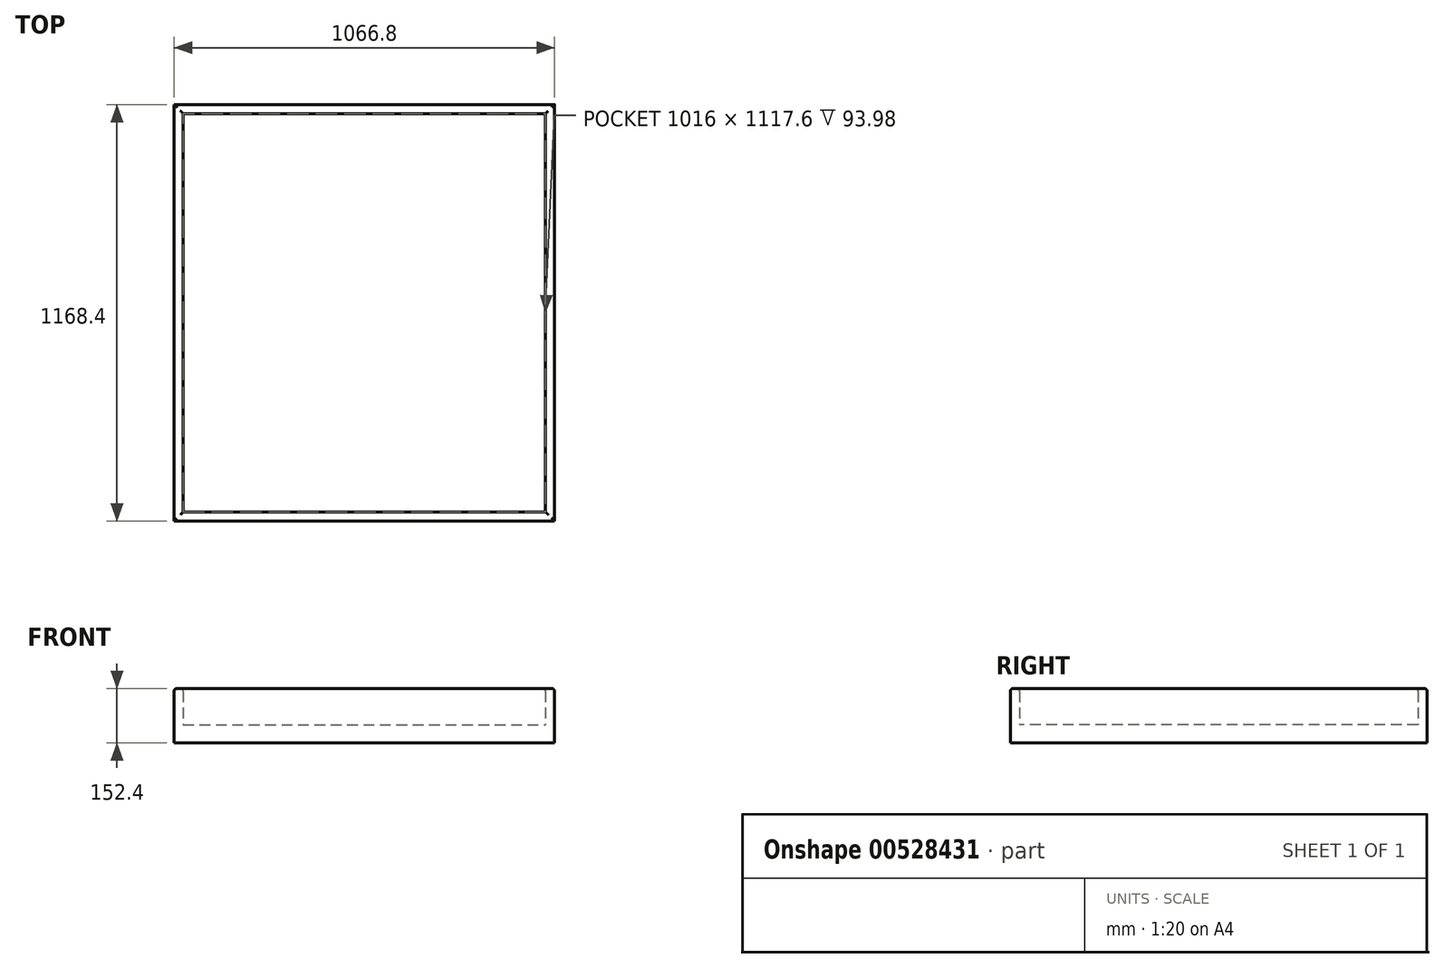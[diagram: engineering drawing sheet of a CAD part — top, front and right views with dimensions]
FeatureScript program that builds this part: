
annotation { "Feature Type Name" : "Feature", "Feature Type Description" : "" }
export const myFeature = defineFeature(function(context is Context, id is Id, definition is map)
    precondition{}
    {
        {
            var Q0;
            Q0=qCreatedBy(makeId("Top.planeOp"),FACE);
            var sketch = newSketch(context, id + "F0", { "sketchPlane" : qUnion([Q0])});
            skLineSegment(sketch, "E0.bottom", {"start": v(-533.4, 584.2) * mm, "end": v(533.4, 584.2) * mm});
            skLineSegment(sketch, "E0.top", {"start": v(-533.4, -584.2) * mm, "end": v(533.4, -584.2) * mm});
            skLineSegment(sketch, "E0.left", {"start": v(-533.4, 584.2) * mm, "end": v(-533.4, -584.2) * mm});
            skLineSegment(sketch, "E0.right", {"start": v(533.4, 584.2) * mm, "end": v(533.4, -584.2) * mm});
            skPoint(sketch, "E0.middle", {"position": v(0, 0) * mm});
            skLineSegment(sketch, "E1.bottom", {"start": v(-508, 558.8) * mm, "end": v(508, 558.8) * mm});
            skLineSegment(sketch, "E1.top", {"start": v(-508, -558.8) * mm, "end": v(508, -558.8) * mm});
            skLineSegment(sketch, "E1.left", {"start": v(-508, 558.8) * mm, "end": v(-508, -558.8) * mm});
            skLineSegment(sketch, "E1.right", {"start": v(508, 558.8) * mm, "end": v(508, -558.8) * mm});
            skSolve(sketch);
        }
        {
            var Q0;
            Q0=makeQuery(id+"F0.imprint","IMPRINT",FACE,{"disambiguationData":[TD([[makeQuery(id+"F0.imprint","IMPRINT",EDGE,{"derivedFrom":sQuery(id+"F0.wireOp",EDGE,"E0.bottom")}),-1.0]])]});
            extrude(context, id + "F1", {"entities" : qUnion([Q0]), "depth" : 152.4 * mm, "offsetDistance" : 25.4 * mm});
        }
        {
            var Q0;
            Q0=makeQuery(id+"F0.imprint","IMPRINT",FACE,{"disambiguationData":[TD([[makeQuery(id+"F0.imprint","IMPRINT",EDGE,{"derivedFrom":sQuery(id+"F0.wireOp",EDGE,"E1.bottom")}),-1.0]])]});
            extrude(context, id + "F2", {"entities" : qUnion([Q0]), "operationType" : NewBodyOperationType.ADD, "depth" : 50.8 * mm, "offsetDistance" : 25.4 * mm});
        }
        {
            var Q0;
            Q0=makeQuery(id+"F1.opExtrude","CAP_EDGE",EDGE,{"disambiguationData":[OSD([sQuery(id+"F0.wireOp",EDGE,"E0.bottom")])],"isStart":false});
            var Q1;
            Q1=makeQuery(id+"F1.opExtrude","CAP_EDGE",EDGE,{"disambiguationData":[OSD([sQuery(id+"F0.wireOp",EDGE,"E0.left")])],"isStart":false});
            var Q2;
            Q2=makeQuery(id+"F1.opExtrude","CAP_EDGE",EDGE,{"disambiguationData":[OSD([sQuery(id+"F0.wireOp",EDGE,"E0.top")])],"isStart":false});
            var Q3;
            Q3=makeQuery(id+"F1.opExtrude","CAP_EDGE",EDGE,{"disambiguationData":[OSD([sQuery(id+"F0.wireOp",EDGE,"E0.right")])],"isStart":false});
            var Q4;
            Q4=makeQuery(id+"F1.opExtrude","CAP_EDGE",EDGE,{"disambiguationData":[OSD([sQuery(id+"F0.wireOp",EDGE,"E1.right")])],"isStart":false});
            var Q5;
            Q5=makeQuery(id+"F1.opExtrude","CAP_EDGE",EDGE,{"disambiguationData":[OSD([sQuery(id+"F0.wireOp",EDGE,"E1.bottom")])],"isStart":false});
            var Q6;
            Q6=makeQuery(id+"F1.opExtrude","CAP_EDGE",EDGE,{"disambiguationData":[OSD([sQuery(id+"F0.wireOp",EDGE,"E1.left")])],"isStart":false});
            var Q7;
            Q7=makeQuery(id+"F1.opExtrude","CAP_EDGE",EDGE,{"disambiguationData":[OSD([sQuery(id+"F0.wireOp",EDGE,"E1.top")])],"isStart":false});
            fillet(context, id + "F3", {"entities" : qUnion([Q0, Q1, Q2, Q3, Q4, Q5, Q6, Q7]), "radius" : 7.62 * mm, "tangentPropagation" : true, "allowEdgeOverflow" : false});
        }
    });
